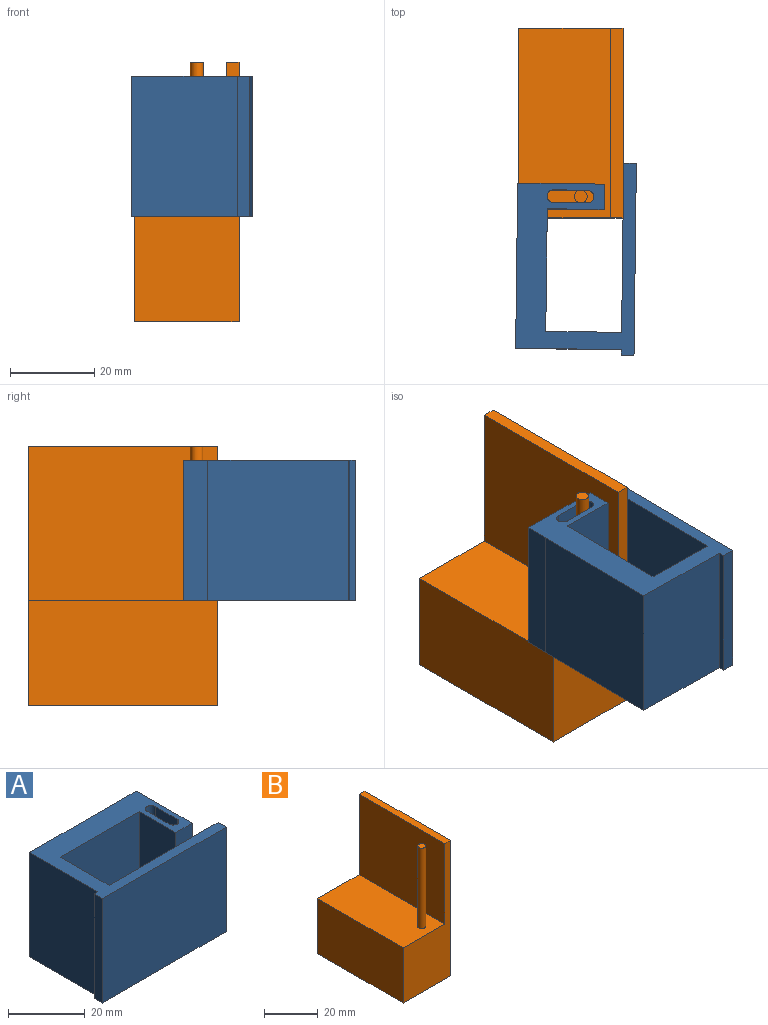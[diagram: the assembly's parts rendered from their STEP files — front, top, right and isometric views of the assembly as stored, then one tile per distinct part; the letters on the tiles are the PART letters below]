
ASSEMBLY  parts=2 mates=2
PART A: 20 faces, bbox 45.5x28x33.2 mm
  f0: plane 33.21x5.87mm, normal (0,1,0), area 194.8mm2, adj f1,f2,f4,f19
  f1: plane 45.51x28.04mm, normal (0,0,1), area 536.1mm2, adj f0,f3,f4,f5,f6,f7,f8,f9
  f2: plane 45.51x28.04mm, normal (0,0,-1), area 536.1mm2, adj f0,f3,f4,f5,f6,f7,f8,f9
  f3: plane 33.21x13.45mm, normal (-1,0,0), area 446.8mm2, adj f1,f2,f9,f17
  f4: plane 33.21x20.49mm, normal (1,0,0), area 680.6mm2, adj f0,f1,f2,f9
  f5: plane 33.21x8.07mm, normal (-1,0,0), area 268.1mm2, adj f1,f2,f6,f8
  f6: cylinder r=1.5mm len=33.21mm, axis (0,0,1), area 156.5mm2, adj f1,f2,f5,f7
  f7: plane 33.21x8.07mm, normal (1,0,0), area 268.1mm2, adj f1,f2,f6,f8
  f8: cylinder r=1.5mm len=33.21mm, axis (0,0,1), area 156.5mm2, adj f1,f2,f5,f7
  f9: plane 33.21x6mm, normal (0,-1,0), area 199.3mm2, adj f1,f2,f3,f4
  f10: plane 33.21x1.39mm, normal (0,1,0), area 46.1mm2, adj f1,f2,f12,f16
  f11: plane 40.03x33.21mm, normal (0,1,0), area 1329.7mm2, adj f1,f2,f13,f15
  f12: plane 33.21x3mm, normal (-1,0,0), area 99.6mm2, adj f1,f2,f10,f14
  f13: plane 33.21x3mm, normal (1,0,0), area 99.6mm2, adj f1,f2,f11,f14
  f14: plane 45.51x33.21mm, normal (0,-1,0), area 1511.4mm2, adj f1,f2,f12,f13
  f15: plane 33.21x17.96mm, normal (1,0,0), area 596.5mm2, adj f1,f2,f11,f17
  f16: plane 33.21x25.04mm, normal (-1,0,0), area 831.7mm2, adj f1,f2,f10,f18
  f17: plane 33.21x29.03mm, normal (0,-1,0), area 964.3mm2, adj f1,f2,f3,f15
  f18: plane 33.25x33.21mm, normal (0,1,0), area 1104.4mm2, adj f1,f2,f16,f19
  f19: plane 33.21x0.04mm, normal (1,0,0), area 1.4mm2, adj f0,f1,f2,f18
PART B: 10 faces, bbox 24.7x44.8x61.5 mm
  f0: plane 44.85x3mm, normal (0,0,1), area 134.5mm2, adj f1,f2,f3,f4
  f1: plane 61.5x24.7mm, normal (0,-1,0), area 727.1mm2, adj f0,f3,f4,f5,f6,f7
  f2: plane 61.5x24.7mm, normal (0,1,0), area 727.1mm2, adj f0,f3,f4,f5,f6,f7
  f3: plane 61.5x44.85mm, normal (1,0,0), area 2758.1mm2, adj f0,f1,f2,f7
  f4: plane 44.85x36.5mm, normal (-1,0,0), area 1636.9mm2, adj f0,f1,f2,f5
  f5: plane 44.85x21.7mm, normal (0,0,1), area 966.3mm2, adj f1,f2,f4,f6,f9
  f6: plane 44.85x25mm, normal (-1,0,0), area 1121.2mm2, adj f1,f2,f5,f7
  f7: plane 44.85x24.7mm, normal (0,0,-1), area 1108mm2, adj f1,f2,f3,f6
  f8: plane 3x3mm, normal (0,0,1), area 7.1mm2, adj f9
  f9: cylinder r=1.5mm len=36.5mm, axis (0,0,-1), area 344mm2, adj f5,f8
PLACE A rot(axis=(0,0,1),89.3deg) t=(-8.98,-16.31,29.93)mm
PLACE B t=(-11.99,4.5,29.93)mm fixed
MATE planar B.f5 <-> A.f2  axis (0,0,1) through (-22.87,5.53,29.93)mm
MATE pin_slot B.f9 <-> A.f2  axis (0,0,1) through (-18.99,-12.02,29.93)mm
